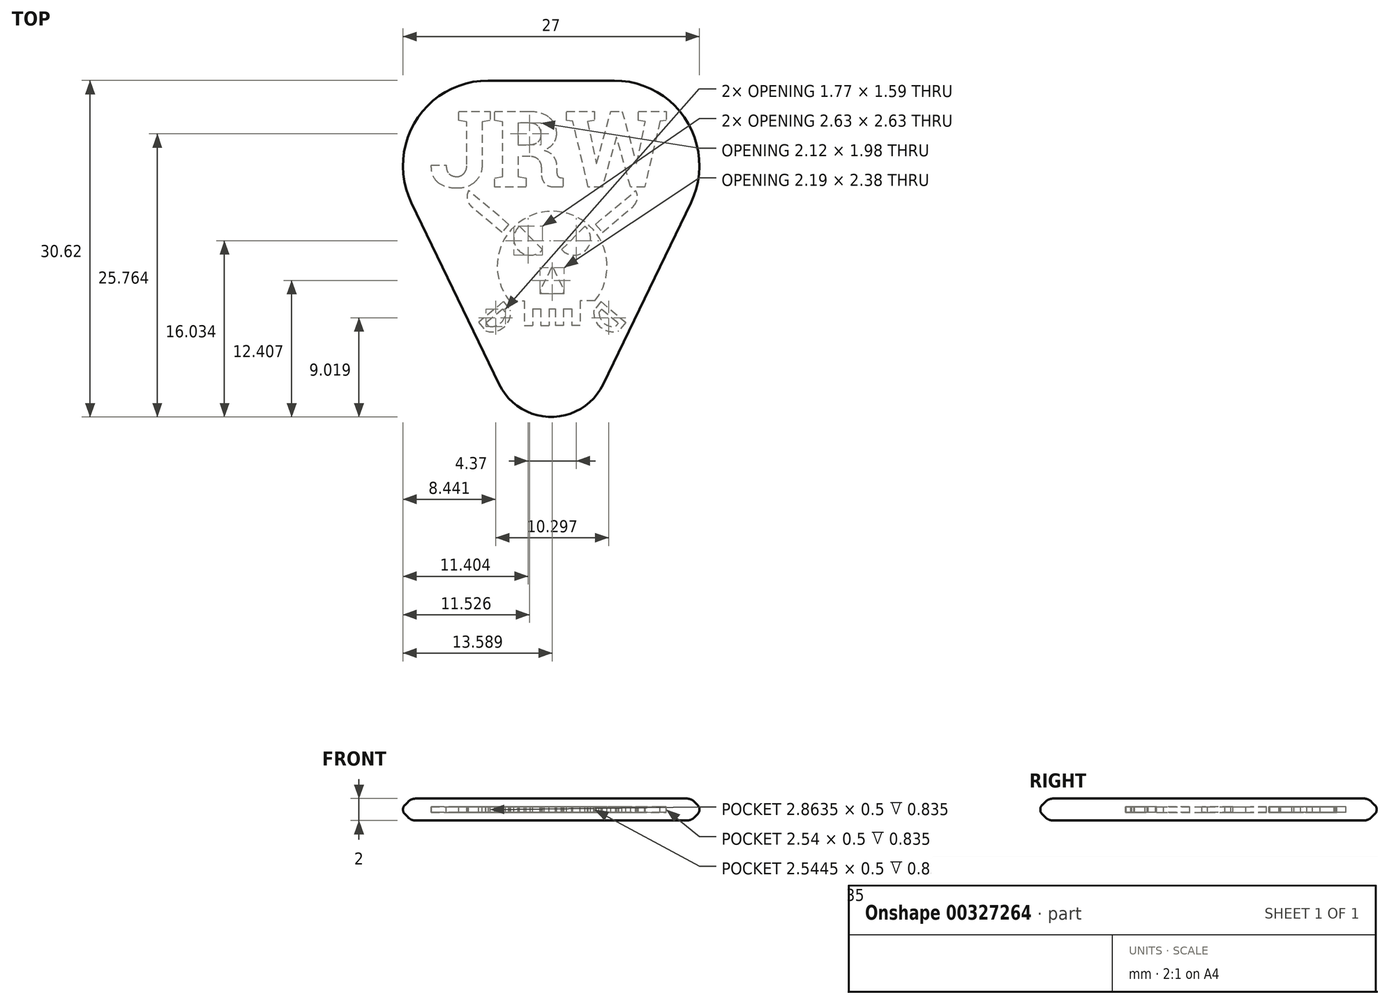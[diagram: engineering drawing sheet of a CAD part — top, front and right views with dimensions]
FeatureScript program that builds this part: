
annotation { "Feature Type Name" : "Feature", "Feature Type Description" : "" }
export const myFeature = defineFeature(function(context is Context, id is Id, definition is map)
    precondition{}
    {
        {
            var Q0;
            Q0=qCreatedBy(makeId("Top.planeOp"),FACE);
            var sketch = newSketch(context, id + "F0", { "sketchPlane" : qUnion([Q0])});
            skLineSegment(sketch, "E0", {"start": v(-5.74, 12.45) * mm, "end": v(5.74, 12.45) * mm});
            skLineSegment(sketch, "E1", {"start": v(12.95, 0.97) * mm, "end": v(4.95, -15.56) * mm});
            skLineSegment(sketch, "E2", {"start": v(-4.95, -15.56) * mm, "end": v(-12.95, 0.97) * mm});
            skPoint(sketch, "E3.visualSharp", {"position": v(-18.5, 12.45) * mm});
            skArc(sketch, "E3.filletArc", {"start": v(-5.74, 12.45) * mm, "mid": v(-12.52, 8.7) * mm, "end": v(-12.95, 0.97) * mm});
            skPoint(sketch, "E4.visualSharp", {"position": v(18.5, 12.45) * mm});
            skArc(sketch, "E4.filletArc", {"start": v(12.95, 0.97) * mm, "mid": v(12.52, 8.7) * mm, "end": v(5.74, 12.45) * mm});
            skPoint(sketch, "E5.visualSharp", {"position": v(0, -25.8) * mm});
            skArc(sketch, "E5.filletArc", {"start": v(-4.95, -15.56) * mm, "mid": v(0, -18.66) * mm, "end": v(4.95, -15.56) * mm});
            skSolve(sketch);
        }
        {
            var Q0;
            Q0=makeQuery(id+"F0.imprint","IMPRINT",FACE,{"disambiguationData":[TD([[makeQuery(id+"F0.imprint","IMPRINT",EDGE,{"derivedFrom":sQuery(id+"F0.wireOp",EDGE,"E0")}),-1.0]])]});
            extrude(context, id + "F1", {"entities" : qUnion([Q0]), "endBound" : BoundingType.SYMMETRIC, "depth" : 2 * mm});
        }
        {
            var Q0;
            Q0=makeQuery(id+"F1.opExtrude","CAP_EDGE",EDGE,{"disambiguationData":[OSD([sQuery(id+"F0.wireOp",EDGE,"E1")])],"isStart":false});
            var Q1;
            Q1=makeQuery(id+"F1.opExtrude","CAP_EDGE",EDGE,{"disambiguationData":[OSD([sQuery(id+"F0.wireOp",EDGE,"E1")])],"isStart":true});
            chamfer(context, id + "F2", {"entities" : qUnion([Q0, Q1]), "chamferType" : ChamferType.OFFSET_ANGLE, "width" : 1 * mm, "oppositeDirection" : false, "angle" : 45 * degree, "tangentPropagation" : true});
        }
        {
            var Q0;
            {var subQ0=sQuery(id+"F0.wireOp",EDGE,"E2");Q0=makeQuery(id+"F2.opChamfer","BLEND_EDGE",EDGE,{"blendedFrom":[makeQuery(id+"F1.opExtrude","CAP_EDGE",EDGE,{"disambiguationData":[OSD([subQ0])],"isStart":false}),makeQuery(id+"F1.opExtrude","CAP_FACE",FACE,{"disambiguationData":[OSD([sQuery(id+"F0.wireOp",EDGE,"E0"),sQuery(id+"F0.wireOp",EDGE,"E1"),subQ0,sQuery(id+"F0.wireOp",EDGE,"E3.filletArc"),sQuery(id+"F0.wireOp",EDGE,"E4.filletArc"),sQuery(id+"F0.wireOp",EDGE,"E5.filletArc")])],"isStart":false})],"blendedInto":[makeQuery(id+"F1.opExtrude","CAP_FACE",FACE,{"disambiguationData":[OSD([sQuery(id+"F0.wireOp",EDGE,"E0"),sQuery(id+"F0.wireOp",EDGE,"E1"),subQ0,sQuery(id+"F0.wireOp",EDGE,"E3.filletArc"),sQuery(id+"F0.wireOp",EDGE,"E4.filletArc"),sQuery(id+"F0.wireOp",EDGE,"E5.filletArc")])],"isStart":false})]});}
            var Q1;
            {var subQ0=sQuery(id+"F0.wireOp",EDGE,"E1");Q1=makeQuery(id+"F2.opChamfer","BLEND_EDGE",EDGE,{"blendedFrom":[makeQuery(id+"F1.opExtrude","CAP_EDGE",EDGE,{"disambiguationData":[OSD([subQ0])],"isStart":true}),makeQuery(id+"F1.opExtrude","CAP_FACE",FACE,{"disambiguationData":[OSD([sQuery(id+"F0.wireOp",EDGE,"E0"),subQ0,sQuery(id+"F0.wireOp",EDGE,"E2"),sQuery(id+"F0.wireOp",EDGE,"E3.filletArc"),sQuery(id+"F0.wireOp",EDGE,"E4.filletArc"),sQuery(id+"F0.wireOp",EDGE,"E5.filletArc")])],"isStart":true})],"blendedInto":[makeQuery(id+"F1.opExtrude","CAP_FACE",FACE,{"disambiguationData":[OSD([sQuery(id+"F0.wireOp",EDGE,"E0"),subQ0,sQuery(id+"F0.wireOp",EDGE,"E2"),sQuery(id+"F0.wireOp",EDGE,"E3.filletArc"),sQuery(id+"F0.wireOp",EDGE,"E4.filletArc"),sQuery(id+"F0.wireOp",EDGE,"E5.filletArc")])],"isStart":true})]});}
            fillet(context, id + "F3", {"entities" : qUnion([Q0, Q1]), "radius" : 1 * mm, "tangentPropagation" : true, "allowEdgeOverflow" : false});
        }
        {
            var Q0;
            Q0=qCreatedBy(makeId("Top.planeOp"),FACE);
            var sketch = newSketch(context, id + "F4", { "sketchPlane" : qUnion([Q0])});
            skText(sketch, "E6", { "text": "JRW", "fontName": "RobotoSlab-Bold.ttf"});
            const initialGuessF4  = {"E6": [-0.01108, 0.0025, 1, 0, 0.007]};
            skSetInitialGuess(sketch, initialGuessF4);
            skSolve(sketch);
        }
        {
            var Q0;
            Q0=qSketchRegion(id+"F4",true);
            extrude(context, id + "F5", {"entities" : qUnion([Q0]), "operationType" : NewBodyOperationType.REMOVE, "endBound" : BoundingType.SYMMETRIC, "oppositeDirection" : true, "depth" : 0.5 * mm});
        }
        {
            var Q0;
            {var subQ0=sQuery(id+"F0.wireOp",EDGE,"E2");Q0=makeQuery(id+"F2.opChamfer","BLEND_EDGE",EDGE,{"blendedFrom":[makeQuery(id+"F1.opExtrude","CAP_EDGE",EDGE,{"disambiguationData":[OSD([subQ0])],"isStart":true}),makeQuery(id+"F1.opExtrude","CAP_EDGE",EDGE,{"disambiguationData":[OSD([subQ0])],"isStart":false})],"blendedInto":[]});}
            fillet(context, id + "F6", {"entities" : qUnion([Q0]), "radius" : 0.6 * mm, "tangentPropagation" : true, "allowEdgeOverflow" : false});
        }
        {
            var Q0;
            Q0=qCreatedBy(makeId("Top.planeOp"),FACE);
            var sketch = newSketch(context, id + "F7", { "sketchPlane" : qUnion([Q0])});
            skArc(sketch, "E7", {"start": v(3.98, -7.83) * mm, "mid": v(0.09, 0.3) * mm, "end": v(-3.8, -7.83) * mm});
            skLineSegment(sketch, "E8", {"start": v(-2.44, -9) * mm, "end": v(-2.44, -10.08) * mm});
            skLineSegment(sketch, "E9", {"start": v(-2.44, -10.08) * mm, "end": v(-1.7, -10.08) * mm});
            skLineSegment(sketch, "E10.MirrorCS", {"start": v(2.62, -10.08) * mm, "end": v(1.87, -10.08) * mm});
            skLineSegment(sketch, "E11.MirrorCS", {"start": v(2.62, -9) * mm, "end": v(2.62, -10.08) * mm});
            skLineSegment(sketch, "E12", {"start": v(-3.8, -7.83) * mm, "end": v(-2.44, -7.83) * mm});
            skLineSegment(sketch, "E13", {"start": v(-2.44, -7.83) * mm, "end": v(-2.44, -9) * mm});
            skLineSegment(sketch, "E14.MirrorCS", {"start": v(3.98, -7.83) * mm, "end": v(2.62, -7.83) * mm});
            skLineSegment(sketch, "E15.MirrorCS", {"start": v(2.62, -7.83) * mm, "end": v(2.62, -9) * mm});
            skArc(sketch, "E16", {"start": v(-2.9, -1.06) * mm, "mid": v(-2.97, -3.25) * mm, "end": v(-0.78, -3.18) * mm});
            skArc(sketch, "E17.MirrorC", {"start": v(3.08, -1.06) * mm, "mid": v(3.15, -3.25) * mm, "end": v(0.96, -3.18) * mm});
            skLineSegment(sketch, "E18", {"start": v(-1.7, -8.58) * mm, "end": v(-1.7, -10.08) * mm});
            skLineSegment(sketch, "E19", {"start": v(-0.94, -8.58) * mm, "end": v(-0.94, -10.08) * mm});
            skLineSegment(sketch, "E20.MirrorCS", {"start": v(1.87, -8.58) * mm, "end": v(1.87, -10.08) * mm});
            skLineSegment(sketch, "E21.MirrorCS", {"start": v(1.12, -8.58) * mm, "end": v(1.12, -10.08) * mm});
            skLineSegment(sketch, "E22", {"start": v(-0.2, -8.58) * mm, "end": v(-0.2, -10.08) * mm});
            skLineSegment(sketch, "E23.MirrorCS", {"start": v(0.37, -8.58) * mm, "end": v(0.37, -10.08) * mm});
            skLineSegment(sketch, "E24.trimOffspring", {"start": v(-0.94, -10.08) * mm, "end": v(-0.2, -10.08) * mm});
            skPoint(sketch, "E25.orphan", {"position": v(0.09, -10.08) * mm});
            skLineSegment(sketch, "E26.trimOffspring", {"start": v(1.12, -10.08) * mm, "end": v(0.37, -10.08) * mm});
            skLineSegment(sketch, "E27", {"start": v(-1.7, -8.58) * mm, "end": v(-0.94, -8.58) * mm});
            skLineSegment(sketch, "E28", {"start": v(-0.2, -8.58) * mm, "end": v(0.37, -8.58) * mm});
            skLineSegment(sketch, "E29", {"start": v(1.12, -8.58) * mm, "end": v(1.87, -8.58) * mm});
            skPoint(sketch, "E30.start.orphan", {"position": v(-1.7, -7.83) * mm});
            skPoint(sketch, "E31.orphan", {"position": v(-0.94, -7.83) * mm});
            skPoint(sketch, "E32.start.orphan", {"position": v(-0.2, -7.83) * mm});
            skPoint(sketch, "E33.orphan", {"position": v(0.37, -7.83) * mm});
            skPoint(sketch, "E34.start.orphan", {"position": v(1.12, -7.83) * mm});
            skPoint(sketch, "E35.orphan", {"position": v(1.87, -7.83) * mm});
            skLineSegment(sketch, "E36", {"start": v(0, -4.87) * mm, "end": v(-0.98, -6.83) * mm});
            skLineSegment(sketch, "E37", {"start": v(-0.76, -7.2) * mm, "end": v(0.09, -7.2) * mm});
            skLineSegment(sketch, "E38.MirrorCS", {"start": v(0.18, -4.87) * mm, "end": v(1.16, -6.83) * mm});
            skLineSegment(sketch, "E39.MirrorCS", {"start": v(0.93, -7.2) * mm, "end": v(0.09, -7.2) * mm});
            skArc(sketch, "E40.filletArc", {"start": v(0.18, -4.87) * mm, "mid": v(0.09, -4.81) * mm, "end": v(0, -4.87) * mm});
            skPoint(sketch, "E41.visualSharp", {"position": v(-1.16, -7.2) * mm});
            skArc(sketch, "E41.filletArc", {"start": v(-0.98, -6.83) * mm, "mid": v(-0.97, -7.07) * mm, "end": v(-0.76, -7.2) * mm});
            skPoint(sketch, "E42.visualSharp", {"position": v(1.34, -7.2) * mm});
            skArc(sketch, "E42.filletArc", {"start": v(0.93, -7.2) * mm, "mid": v(1.15, -7.07) * mm, "end": v(1.16, -6.83) * mm});
            skLineSegment(sketch, "E43", {"start": v(4.04, -0.88) * mm, "end": v(7.7, 2.19) * mm});
            skLineSegment(sketch, "E44", {"start": v(4.66, -1.61) * mm, "end": v(7.41, 0.7) * mm});
            skArc(sketch, "E45", {"start": v(7.41, 0.7) * mm, "mid": v(7.82, 1.4) * mm, "end": v(7.7, 2.19) * mm});
            skLineSegment(sketch, "E46", {"start": v(4.04, -0.88) * mm, "end": v(-3.7, -7.37) * mm, "construction": true});
            skLineSegment(sketch, "E47", {"start": v(-6.62, -9.82) * mm, "end": v(-5.98, -10.59) * mm});
            skLineSegment(sketch, "E48", {"start": v(4.04, -0.88) * mm, "end": v(4.66, -1.61) * mm});
            skLineSegment(sketch, "E49", {"start": v(-4.35, -7.92) * mm, "end": v(-3.71, -8.69) * mm});
            skLineSegment(sketch, "E50.trimOffspring", {"start": v(-4.35, -7.92) * mm, "end": v(-5.74, -9.08) * mm, "construction": true});
            skLineSegment(sketch, "E51.trimOffspring", {"start": v(-4.35, -7.92) * mm, "end": v(-6.62, -9.82) * mm});
            skPoint(sketch, "E52", {"position": v(-5.98, -10.59) * mm});
            skPoint(sketch, "E53.orphan", {"position": v(-5.33, -11.35) * mm});
            skArc(sketch, "E54", {"start": v(-5.98, -10.59) * mm, "mid": v(-4.32, -10.26) * mm, "end": v(-3.71, -8.69) * mm});
            skLineSegment(sketch, "E55.0", {"start": v(-4.41, -8.6) * mm, "end": v(-5.94, -9.88) * mm});
            skLineSegment(sketch, "E55.1", {"start": v(-4.41, -8.6) * mm, "end": v(-4.18, -8.88) * mm});
            skArc(sketch, "E55.2", {"start": v(-5.7, -10.16) * mm, "mid": v(-4.63, -9.89) * mm, "end": v(-4.18, -8.88) * mm});
            skLineSegment(sketch, "E55.3", {"start": v(-5.94, -9.88) * mm, "end": v(-5.7, -10.16) * mm});
            skLineSegment(sketch, "E56.MirrorCS", {"start": v(4.6, -8.6) * mm, "end": v(4.36, -8.88) * mm});
            skLineSegment(sketch, "E57.MirrorCS", {"start": v(6.12, -9.88) * mm, "end": v(5.88, -10.16) * mm});
            skLineSegment(sketch, "E58.MirrorCS", {"start": v(4.53, -7.92) * mm, "end": v(5.92, -9.08) * mm, "construction": true});
            skArc(sketch, "E59.MirrorCS", {"start": v(6.15, -10.59) * mm, "mid": v(4.5, -10.26) * mm, "end": v(3.9, -8.69) * mm});
            skLineSegment(sketch, "E60.MirrorCS", {"start": v(4.53, -7.92) * mm, "end": v(6.8, -9.82) * mm});
            skPoint(sketch, "E61.MirrorP", {"position": v(6.15, -10.59) * mm});
            skLineSegment(sketch, "E62.MirrorCS", {"start": v(4.6, -8.6) * mm, "end": v(6.12, -9.88) * mm});
            skLineSegment(sketch, "E63.MirrorCS", {"start": v(4.53, -7.92) * mm, "end": v(3.9, -8.69) * mm});
            skArc(sketch, "E64.MirrorCS", {"start": v(5.88, -10.16) * mm, "mid": v(4.8, -9.89) * mm, "end": v(4.36, -8.88) * mm});
            skPoint(sketch, "E65.MirrorP", {"position": v(5.51, -11.35) * mm});
            skLineSegment(sketch, "E66.MirrorCS", {"start": v(6.8, -9.82) * mm, "end": v(6.15, -10.59) * mm});
            skLineSegment(sketch, "E67.MirrorCS", {"start": v(-4.48, -1.61) * mm, "end": v(-7.24, 0.7) * mm});
            skArc(sketch, "E68.MirrorCS", {"start": v(-7.24, 0.7) * mm, "mid": v(-7.64, 1.4) * mm, "end": v(-7.51, 2.19) * mm});
            skLineSegment(sketch, "E69.MirrorCS", {"start": v(-3.86, -0.88) * mm, "end": v(-7.51, 2.19) * mm});
            skLineSegment(sketch, "E70.MirrorCS", {"start": v(-3.86, -0.88) * mm, "end": v(-4.48, -1.61) * mm});
            skPoint(sketch, "E71", {"position": v(0.09, -4.2) * mm});
            skLineSegment(sketch, "E72", {"start": v(-2.9, -1.06) * mm, "end": v(-0.78, -3.18) * mm});
            skLineSegment(sketch, "E73.MirrorCS", {"start": v(3.08, -1.06) * mm, "end": v(0.96, -3.18) * mm});
            skSolve(sketch);
        }
        {
            var Q0;
            Q0=qSketchRegion(id+"F7",true);
            var Q1;
            Q1=makeQuery(id+"F7.imprint","IMPRINT",FACE,{"disambiguationData":[TD([[makeQuery(id+"F7.imprint","IMPRINT",EDGE,{"derivedFrom":sQuery(id+"F7.wireOp",EDGE,"b4bf5cf7-47f6-4e07-859f-e1e6065c9dbf.0")}),-1.0]])]});
            var Q2;
            Q2=makeQuery(id+"F7.imprint","IMPRINT",FACE,{"disambiguationData":[TD([[makeQuery(id+"F7.imprint","IMPRINT",EDGE,{"derivedFrom":sQuery(id+"F7.wireOp",EDGE,"6f85d2ec-8929-457e-84c4-58013a10ac05.0")}),-1.0]])]});
            extrude(context, id + "F8", {"entities" : qUnion([Q0, Q1, Q2]), "operationType" : NewBodyOperationType.REMOVE, "endBound" : BoundingType.SYMMETRIC, "oppositeDirection" : true, "depth" : 0.5 * mm, "offsetDistance" : 25 * mm});
        }
    });
